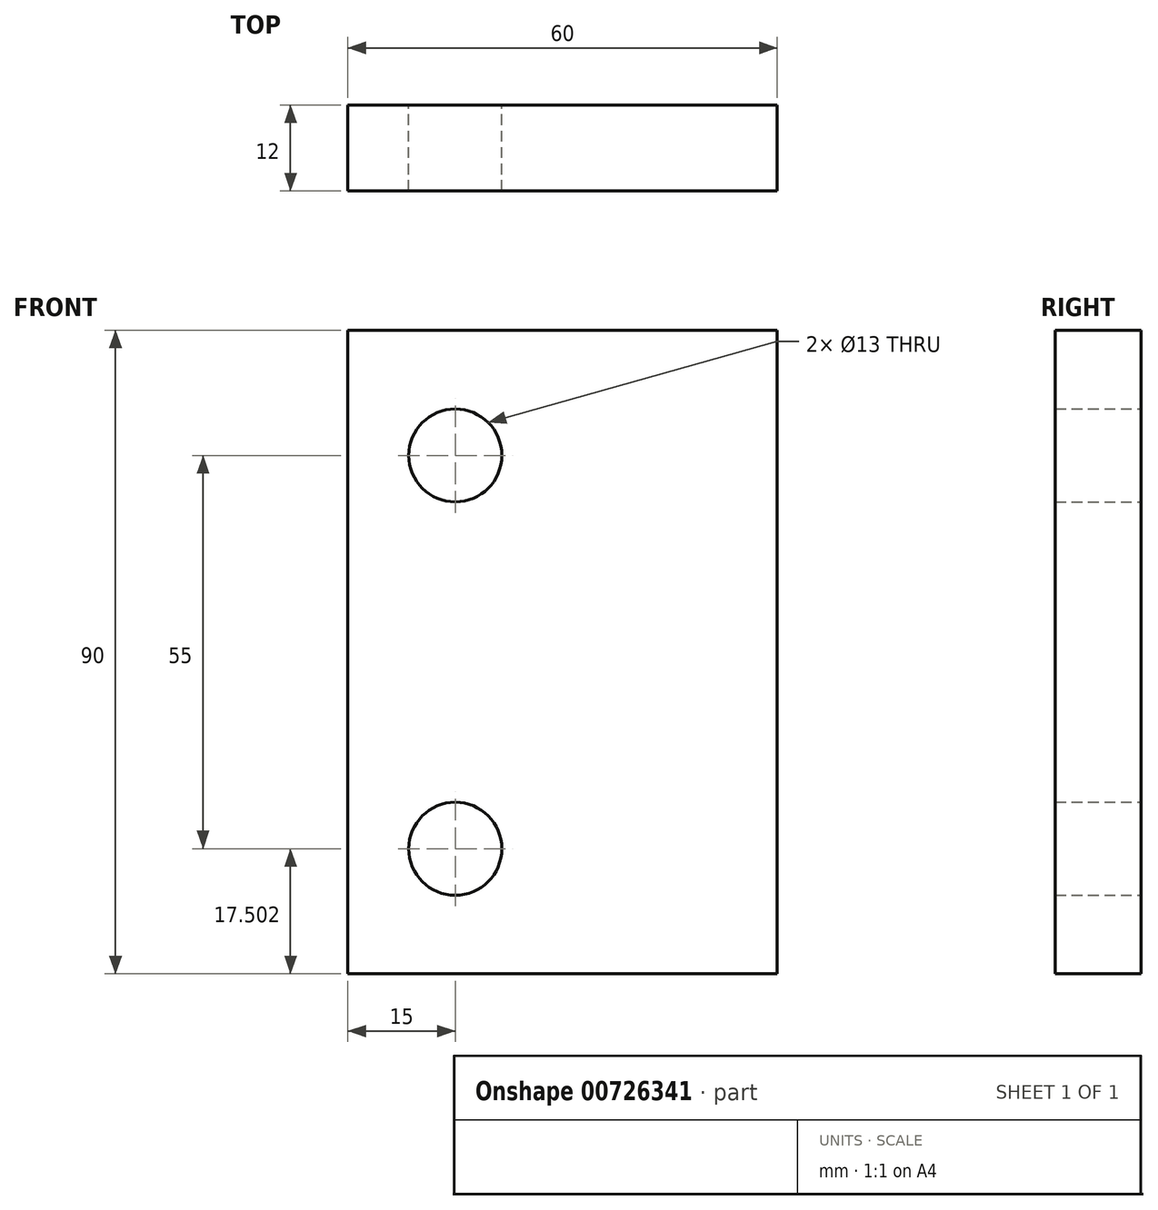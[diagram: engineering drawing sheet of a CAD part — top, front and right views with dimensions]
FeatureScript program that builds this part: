
annotation { "Feature Type Name" : "Feature", "Feature Type Description" : "" }
export const myFeature = defineFeature(function(context is Context, id is Id, definition is map)
    precondition{}
    {
        {
            var Q0;
            Q0=qCreatedBy(makeId("Front.planeOp"),FACE);
            var sketch = newSketch(context, id + "F0", { "sketchPlane" : qUnion([Q0])});
            skLineSegment(sketch, "E0.bottom", {"start": v(-39.58, 80.41) * mm, "end": v(20.42, 80.41) * mm});
            skLineSegment(sketch, "E0.top", {"start": v(-39.58, -9.59) * mm, "end": v(20.42, -9.59) * mm});
            skLineSegment(sketch, "E0.left", {"start": v(-39.58, 80.41) * mm, "end": v(-39.58, -9.59) * mm});
            skLineSegment(sketch, "E0.right", {"start": v(20.42, 80.41) * mm, "end": v(20.42, -9.59) * mm});
            skLineSegment(sketch, "E1", {"start": v(-24.58, 90.91) * mm, "end": v(-24.58, -31.76) * mm, "construction": true});
            skPoint(sketch, "E2", {"position": v(-24.58, 62.91) * mm});
            skPoint(sketch, "E3", {"position": v(-24.58, 7.91) * mm});
            skLineSegment(sketch, "E4", {"start": v(-62.14, 35.41) * mm, "end": v(59.06, 35.41) * mm, "construction": true});
            skSolve(sketch);
        }
        {
            var Q0;
            Q0 = qSketchRegion(id + "F0", true);
            var Q1;
            Q1=makeQuery(id+"F0.imprint","IMPRINT",FACE,{"disambiguationData":[TD([[makeQuery(id+"F0.imprint","IMPRINT",EDGE,{"derivedFrom":sQuery(id+"F0.wireOp",EDGE,"E0.bottom")}),-1.0]])]});
            extrude(context, id + "F1", {"entities" : qUnion([Q0, Q1]), "depth" : 12 * mm, "offsetDistance" : 25 * mm});
        }
        {
            var Q0;
            Q0=sQuery(id+"F0.wireOp",VERTEX,"E2");
            var Q1;
            Q1=sQuery(id+"F0.wireOp",VERTEX,"E3");
            var Q2;
            Q2=makeQuery(id+"F1.opExtrude","SWEPT_BODY",BODY,{"disambiguationData":[OSD([sQuery(id+"F0.wireOp",EDGE,"E0.bottom"),sQuery(id+"F0.wireOp",EDGE,"E0.top"),sQuery(id+"F0.wireOp",EDGE,"E0.left"),sQuery(id+"F0.wireOp",EDGE,"E0.right")])]});
            hole(context, id + "F2", {"style" : HoleStyle.SIMPLE, "endStyle" : HoleEndStyle.THROUGH, "oppositeDirection" : true, "holeDiameter" : 13 * mm, "majorDiameter" : 5 * mm, "isTappedThrough" : true, "tappedDepth" : 12 * mm, "tapClearance" : 3, "locations" : qUnion([Q0, Q1]), "scope" : qUnion([Q2])});
        }
    });
